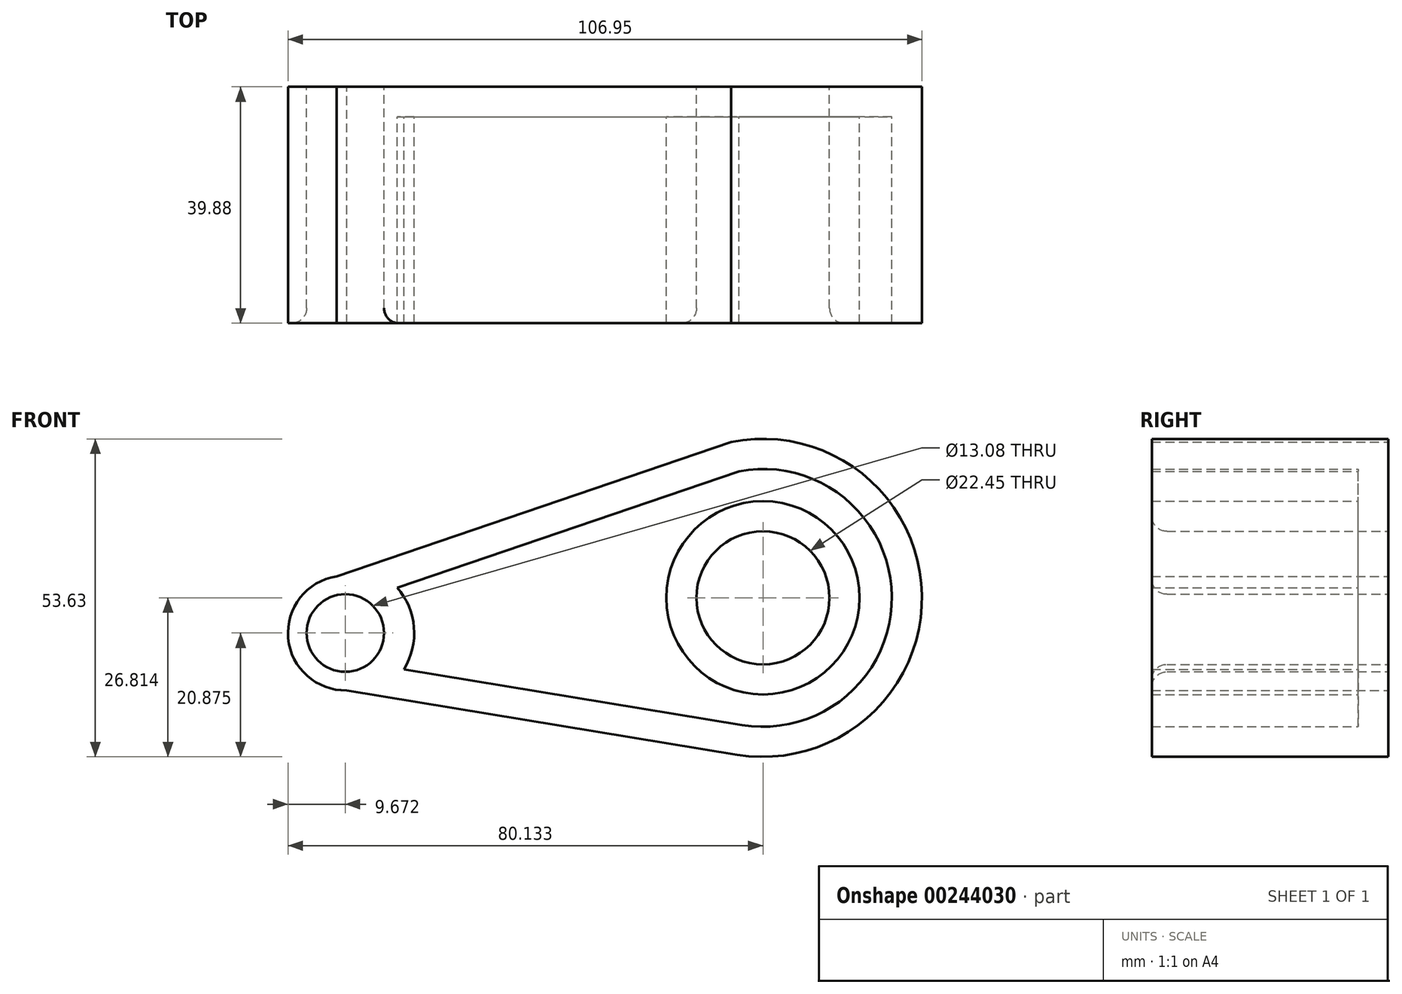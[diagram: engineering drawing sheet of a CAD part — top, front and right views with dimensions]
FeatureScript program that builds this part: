
annotation { "Feature Type Name" : "Feature", "Feature Type Description" : "" }
export const myFeature = defineFeature(function(context is Context, id is Id, definition is map)
    precondition{}
    {
        {
            var Q0;
            Q0=qCreatedBy(makeId("Front.planeOp"),FACE);
            var sketch = newSketch(context, id + "F0", { "sketchPlane" : qUnion([Q0])});
            skArc(sketch, "E0", {"start": v(-47.02, 49.72) * mm, "mid": v(-55.2, 39.3) * mm, "end": v(-45.31, 30.5) * mm});
            skArc(sketch, "E1", {"start": v(20.54, 19.64) * mm, "mid": v(51.43, 50) * mm, "end": v(13.12, 70.2) * mm});
            skLineSegment(sketch, "E2", {"start": v(-47.02, 49.72) * mm, "end": v(19.55, 72.38) * mm});
            skLineSegment(sketch, "E3", {"start": v(-45.31, 30.5) * mm, "end": v(20.54, 19.64) * mm});
            skCircle(sketch, "E4", {"center": v(-45.56, 40.16) * mm, "radius": 6.54 * mm});
            skCircle(sketch, "E5", {"center": v(24.9, 46.1) * mm, "radius": 11.22 * mm});
            skSolve(sketch);
        }
        {
            var Q0;
            {var subQ4=sQuery(id+"F0.wireOp",EDGE,"E0");Q0=makeQuery(id+"F0.imprint","IMPRINT",FACE,{"disambiguationData":[TD([[makeQuery(id+"F0.imprint","IMPRINT",EDGE,{"derivedFrom":subQ4}),1.0]])]});}
            extrude(context, id + "F1", {"entities" : qUnion([Q0]), "depth" : 39.88 * mm});
        }
        {
            var Q0;
            Q0=makeQuery(id+"F1.opExtrude","CAP_EDGE",EDGE,{"disambiguationData":[OSD([sQuery(id+"F0.wireOp",EDGE,"E5")])],"isStart":false});
            fillet(context, id + "F2", {"entities" : qUnion([Q0]), "radius" : 2.54 * mm, "tangentPropagation" : true, "allowEdgeOverflow" : false});
        }
        {
            var Q0;
            Q0=makeQuery(id+"F1.opExtrude","CAP_EDGE",EDGE,{"disambiguationData":[OSD([sQuery(id+"F0.wireOp",EDGE,"E4")])],"isStart":false});
            fillet(context, id + "F3", {"entities" : qUnion([Q0]), "radius" : 2.54 * mm, "tangentPropagation" : true, "allowEdgeOverflow" : false});
        }
        {
            var Q0;
            Q0=makeQuery(id+"F1.opExtrude","CAP_FACE",FACE,{"disambiguationData":[OSD([sQuery(id+"F0.wireOp",EDGE,"E0"),sQuery(id+"F0.wireOp",EDGE,"E1"),sQuery(id+"F0.wireOp",EDGE,"E2"),sQuery(id+"F0.wireOp",EDGE,"E3"),sQuery(id+"F0.wireOp",EDGE,"E4"),sQuery(id+"F0.wireOp",EDGE,"E5")])],"isStart":false});
            shell(context, id + "F4", {"entities" : qUnion([Q0]), "thickness" : 5.08 * mm});
        }
    });
